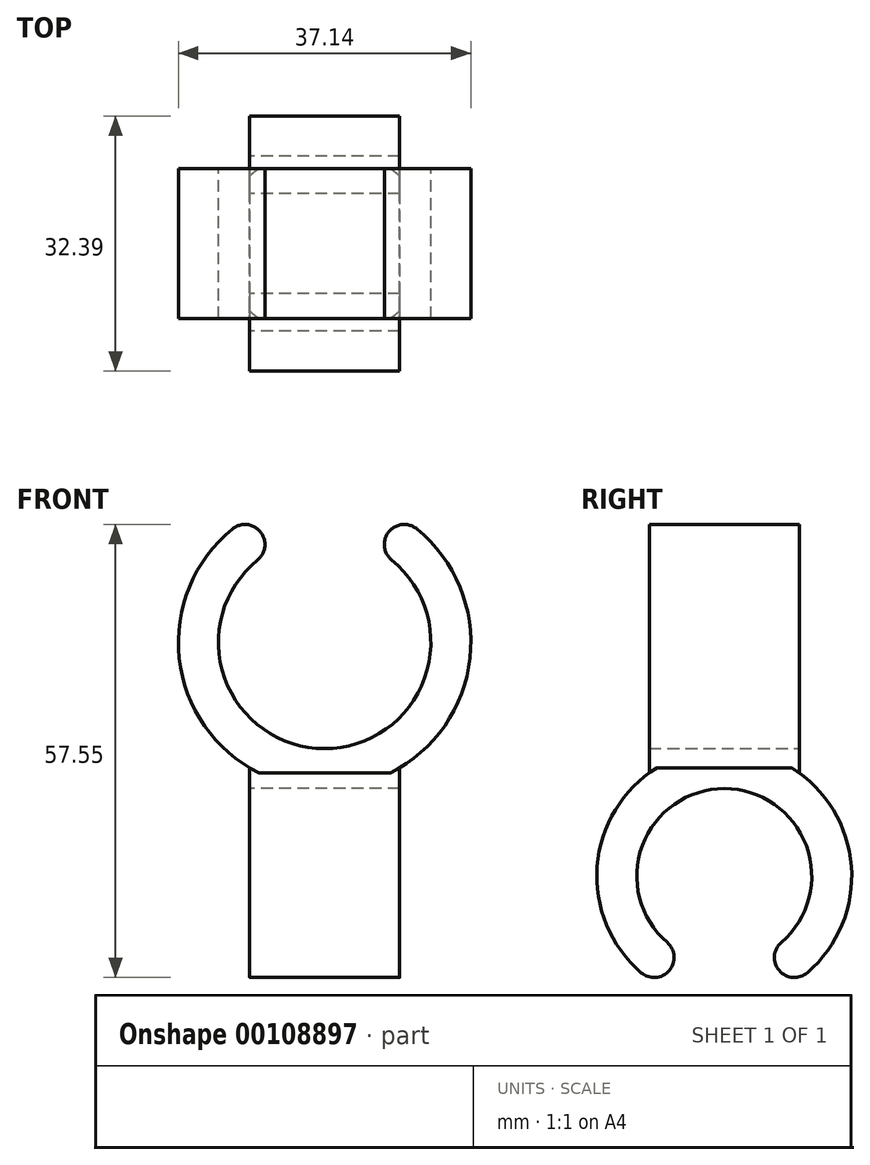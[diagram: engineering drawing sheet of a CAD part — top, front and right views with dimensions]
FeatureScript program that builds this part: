
annotation { "Feature Type Name" : "Feature", "Feature Type Description" : "" }
export const myFeature = defineFeature(function(context is Context, id is Id, definition is map)
    precondition{}
    {
        {
            var Q0;
            Q0=qCreatedBy(makeId("Front.planeOp"),FACE);
            var sketch = newSketch(context, id + "F0", { "sketchPlane" : qUnion([Q0])});
            skArc(sketch, "E0", {"start": v(-8.51, 10.47) * mm, "mid": v(0, -13.5) * mm, "end": v(8.51, 10.47) * mm});
            skArc(sketch, "E1", {"start": v(-11.72, 14.41) * mm, "mid": v(0, -18.57) * mm, "end": v(11.72, 14.41) * mm});
            skLineSegment(sketch, "E2", {"start": v(7.92, 13.71) * mm, "end": v(7.92, 13.71) * mm});
            skLineSegment(sketch, "E3", {"start": v(-7.92, 13.71) * mm, "end": v(-7.92, 13.71) * mm});
            skPoint(sketch, "E4.visualSharp", {"position": v(-6.75, 11.69) * mm});
            skArc(sketch, "E4.filletArc", {"start": v(-8.51, 10.47) * mm, "mid": v(-7.62, 11.98) * mm, "end": v(-7.92, 13.71) * mm});
            skPoint(sketch, "E5.visualSharp", {"position": v(-9.29, 16.09) * mm});
            skArc(sketch, "E5.filletArc", {"start": v(-7.92, 13.71) * mm, "mid": v(-9.65, 14.94) * mm, "end": v(-11.72, 14.41) * mm});
            skPoint(sketch, "E6.visualSharp", {"position": v(6.75, 11.69) * mm});
            skArc(sketch, "E6.filletArc", {"start": v(7.92, 13.71) * mm, "mid": v(7.62, 11.98) * mm, "end": v(8.51, 10.47) * mm});
            skPoint(sketch, "E7.visualSharp", {"position": v(9.29, 16.09) * mm});
            skArc(sketch, "E7.filletArc", {"start": v(11.72, 14.41) * mm, "mid": v(9.65, 14.94) * mm, "end": v(7.92, 13.71) * mm});
            skSolve(sketch);
        }
        {
            var Q0;
            Q0=makeQuery(id+"F0.imprint","IMPRINT",FACE,{"disambiguationData":[TD([[makeQuery(id+"F0.imprint","IMPRINT",EDGE,{"derivedFrom":sQuery(id+"F0.wireOp",EDGE,"E0")}),-1.0]])]});
            extrude(context, id + "F1", {"entities" : qUnion([Q0]), "depth" : 19.05 * mm});
        }
        {
            var Q0;
            Q0=qCreatedBy(makeId("Right.planeOp"),FACE);
            var sketch = newSketch(context, id + "F2", { "sketchPlane" : qUnion([Q0])});
            skArc(sketch, "E8", {"start": v(-2.28, -38.1) * mm, "mid": v(-9.53, -18.57) * mm, "end": v(-16.77, -38.1) * mm});
            skLineSegment(sketch, "E9.0.0", {"start": v(0, -18.57) * mm, "end": v(0, -16.6) * mm});
            skLineSegment(sketch, "E9.0.1", {"start": v(0, 14.41) * mm, "end": v(-19.05, 14.41) * mm});
            skLineSegment(sketch, "E9.0.2", {"start": v(-19.05, -16.6) * mm, "end": v(-19.05, -18.57) * mm});
            skArc(sketch, "E10", {"start": v(1.04, -41.96) * mm, "mid": v(-9.53, -13.5) * mm, "end": v(-20.09, -41.96) * mm});
            skLineSegment(sketch, "E11", {"start": v(-2.82, -41.3) * mm, "end": v(-2.82, -41.3) * mm});
            skLineSegment(sketch, "E12", {"start": v(-16.23, -41.3) * mm, "end": v(-16.23, -41.3) * mm});
            skPoint(sketch, "E13.visualSharp", {"position": v(-15.08, -39.3) * mm});
            skArc(sketch, "E13.filletArc", {"start": v(-16.23, -41.3) * mm, "mid": v(-15.93, -39.6) * mm, "end": v(-16.77, -38.1) * mm});
            skPoint(sketch, "E14.visualSharp", {"position": v(-17.62, -43.7) * mm});
            skArc(sketch, "E14.filletArc", {"start": v(-20.09, -41.96) * mm, "mid": v(-18, -42.54) * mm, "end": v(-16.23, -41.3) * mm});
            skPoint(sketch, "E15.visualSharp", {"position": v(-3.97, -39.3) * mm});
            skArc(sketch, "E15.filletArc", {"start": v(-2.28, -38.1) * mm, "mid": v(-3.12, -39.6) * mm, "end": v(-2.82, -41.3) * mm});
            skPoint(sketch, "E16.visualSharp", {"position": v(-1.43, -43.7) * mm});
            skArc(sketch, "E16.filletArc", {"start": v(-2.82, -41.3) * mm, "mid": v(-1.04, -42.54) * mm, "end": v(1.04, -41.96) * mm});
            skPoint(sketch, "E9.0.3.end.orphan", {"position": v(0, 14.41) * mm});
            skPoint(sketch, "E9.0.3.start.orphan", {"position": v(-19.05, 14.41) * mm});
            skSolve(sketch);
        }
        {
            var Q0;
            Q0=makeQuery(id+"F2.imprint","IMPRINT",FACE,{"disambiguationData":[TD([[makeQuery(id+"F2.imprint","IMPRINT",EDGE,{"derivedFrom":sQuery(id+"F2.wireOp",EDGE,"E8")}),-1.0]])]});
            extrude(context, id + "F3", {"entities" : qUnion([Q0]), "operationType" : NewBodyOperationType.ADD, "depth" : 9.52 * mm});
        }
        {
            var Q0;
            Q0=makeQuery(id+"F2.imprint","IMPRINT",FACE,{"disambiguationData":[TD([[makeQuery(id+"F2.imprint","IMPRINT",EDGE,{"derivedFrom":sQuery(id+"F2.wireOp",EDGE,"E8")}),-1.0]])]});
            extrude(context, id + "F4", {"entities" : qUnion([Q0]), "operationType" : NewBodyOperationType.ADD, "oppositeDirection" : true, "depth" : 9.52 * mm});
        }
    });
